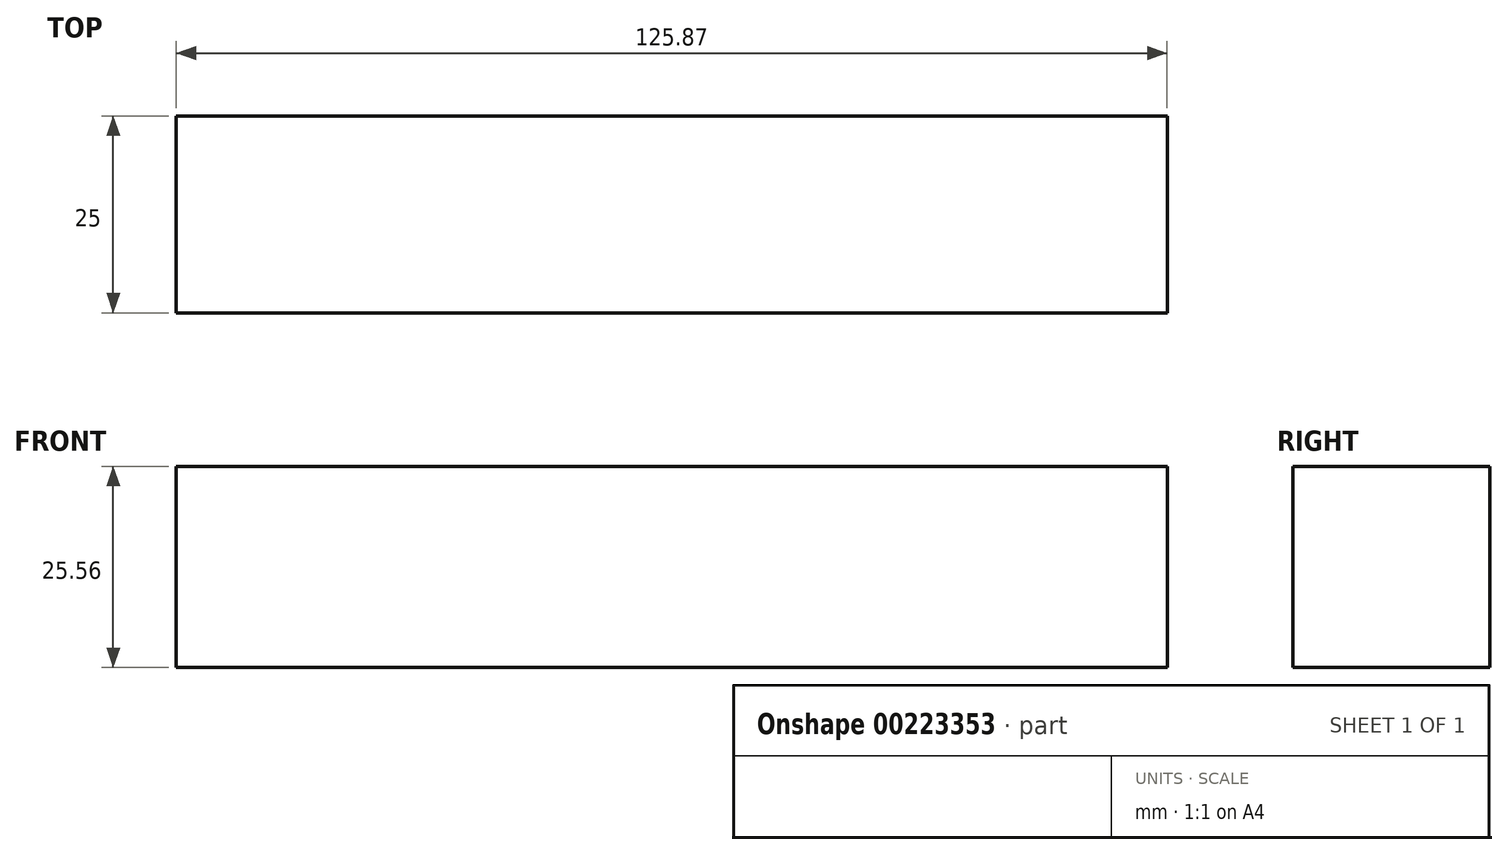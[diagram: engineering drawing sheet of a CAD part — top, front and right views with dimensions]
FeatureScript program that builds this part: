
annotation { "Feature Type Name" : "Feature", "Feature Type Description" : "" }
export const myFeature = defineFeature(function(context is Context, id is Id, definition is map)
    precondition{}
    {
        {
            var Q0;
            Q0=qCreatedBy(makeId("Front.planeOp"),FACE);
            var sketch = newSketch(context, id + "F0", { "sketchPlane" : qUnion([Q0])});
            skLineSegment(sketch, "E0.bottom", {"start": v(82.16, 29.88) * mm, "end": v(-43.71, 29.88) * mm});
            skLineSegment(sketch, "E0.top", {"start": v(82.16, 55.44) * mm, "end": v(-43.71, 55.44) * mm});
            skLineSegment(sketch, "E0.left", {"start": v(82.16, 29.88) * mm, "end": v(82.16, 55.44) * mm});
            skLineSegment(sketch, "E0.right", {"start": v(-43.71, 29.88) * mm, "end": v(-43.71, 55.44) * mm});
            skPoint(sketch, "E0.middle", {"position": v(19.22, 42.66) * mm});
            skSolve(sketch);
        }
        {
            var Q0;
            Q0=makeQuery(id+"F0.imprint","IMPRINT",FACE,{"disambiguationData":[TD([[makeQuery(id+"F0.imprint","IMPRINT",EDGE,{"derivedFrom":sQuery(id+"F0.wireOp",EDGE,"E0.bottom")}),-1.0]])]});
            extrude(context, id + "F1", {"entities" : qUnion([Q0]), "depth" : 25 * mm});
        }
    });
